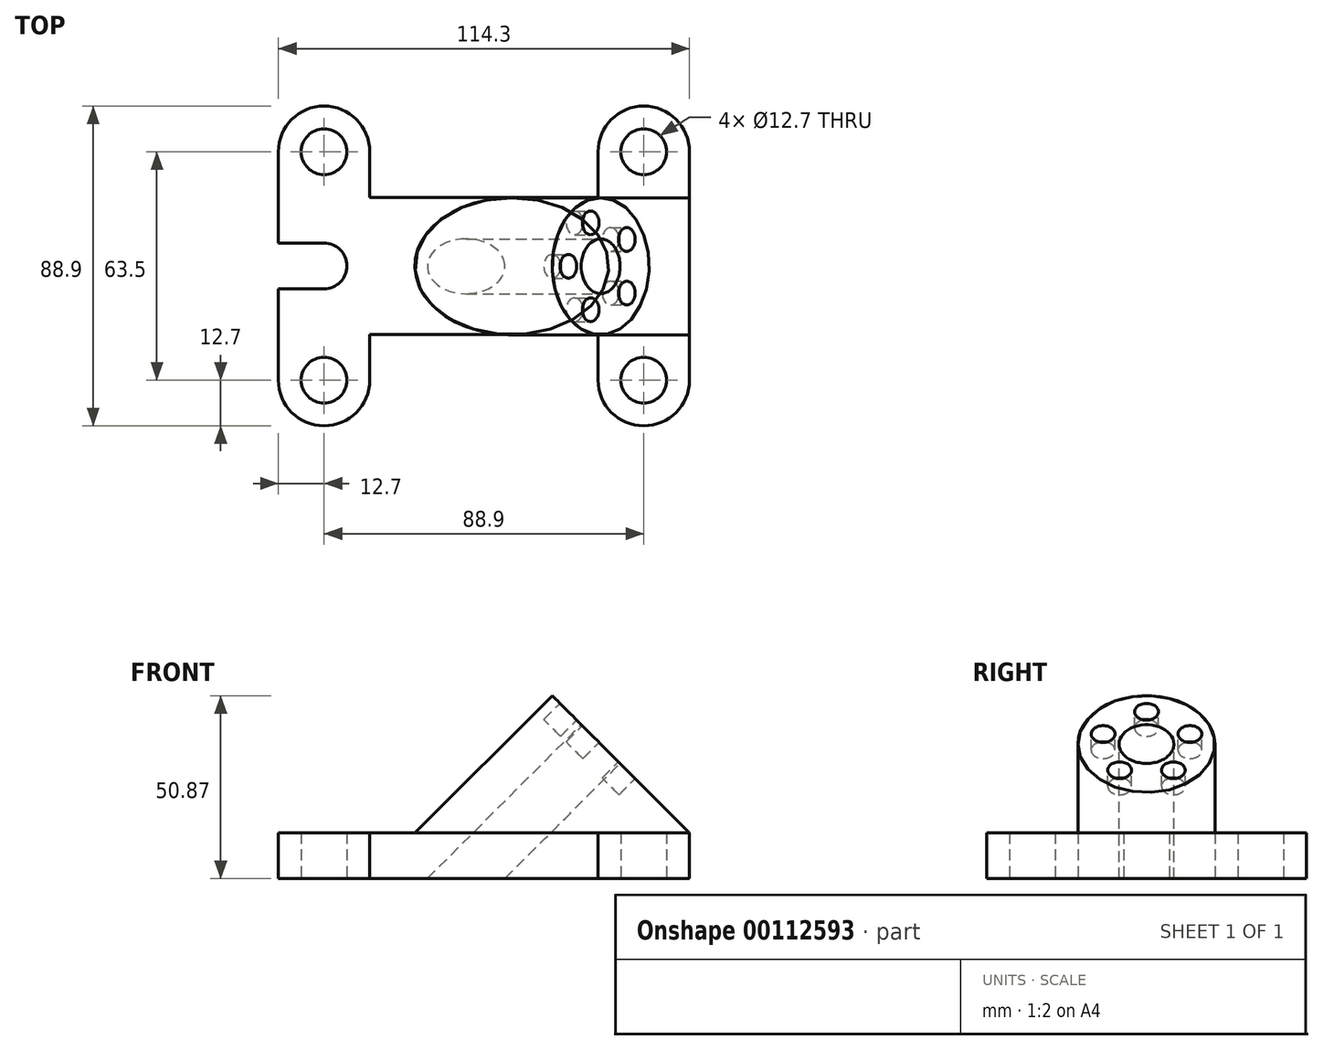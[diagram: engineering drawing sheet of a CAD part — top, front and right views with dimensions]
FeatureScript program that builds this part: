
annotation { "Feature Type Name" : "Feature", "Feature Type Description" : "" }
export const myFeature = defineFeature(function(context is Context, id is Id, definition is map)
    precondition{}
    {
        {
            var Q0;
            Q0=qCreatedBy(makeId("Top.planeOp"),FACE);
            var sketch = newSketch(context, id + "F0", { "sketchPlane" : qUnion([Q0])});
            skLineSegment(sketch, "E0", {"start": v(114.3, 63.5) * mm, "end": v(114.3, 0) * mm});
            skLineSegment(sketch, "E1", {"start": v(0, 38.1) * mm, "end": v(0, 63.5) * mm});
            skLineSegment(sketch, "E2", {"start": v(0, 38.1) * mm, "end": v(12.7, 38.1) * mm});
            skLineSegment(sketch, "E3", {"start": v(0, 0) * mm, "end": v(0, 25.4) * mm});
            skLineSegment(sketch, "E4", {"start": v(0, 25.4) * mm, "end": v(12.7, 25.4) * mm});
            skLineSegment(sketch, "E5", {"start": v(25.4, 63.5) * mm, "end": v(25.4, 50.8) * mm});
            skLineSegment(sketch, "E6", {"start": v(25.4, 50.8) * mm, "end": v(88.9, 50.8) * mm});
            skLineSegment(sketch, "E7", {"start": v(88.9, 50.8) * mm, "end": v(88.9, 63.5) * mm});
            skLineSegment(sketch, "E8", {"start": v(25.4, 0) * mm, "end": v(25.4, 12.7) * mm});
            skLineSegment(sketch, "E9", {"start": v(25.4, 12.7) * mm, "end": v(88.9, 12.7) * mm});
            skLineSegment(sketch, "E10", {"start": v(88.9, 12.7) * mm, "end": v(88.9, 0) * mm});
            skArc(sketch, "E11", {"start": v(25.4, 63.5) * mm, "mid": v(12.7, 76.2) * mm, "end": v(0, 63.5) * mm});
            skArc(sketch, "E12", {"start": v(114.3, 63.5) * mm, "mid": v(101.6, 76.2) * mm, "end": v(88.9, 63.5) * mm});
            skArc(sketch, "E13", {"start": v(88.9, 0) * mm, "mid": v(101.6, -12.7) * mm, "end": v(114.3, 0) * mm});
            skArc(sketch, "E14", {"start": v(0, 0) * mm, "mid": v(12.7, -12.7) * mm, "end": v(25.4, 0) * mm});
            skArc(sketch, "E15", {"start": v(12.7, 25.4) * mm, "mid": v(19.05, 31.75) * mm, "end": v(12.7, 38.1) * mm});
            skCircle(sketch, "E16", {"center": v(12.7, 63.5) * mm, "radius": 6.35 * mm});
            skCircle(sketch, "E17", {"center": v(101.6, 63.5) * mm, "radius": 6.35 * mm});
            skCircle(sketch, "E18", {"center": v(101.6, 0) * mm, "radius": 6.35 * mm});
            skCircle(sketch, "E19", {"center": v(12.7, 0) * mm, "radius": 6.35 * mm});
            skPoint(sketch, "E20", {"position": v(114.3, 31.75) * mm});
            skLineSegment(sketch, "E21", {"start": v(0, 38.1) * mm, "end": v(0, 25.4) * mm, "construction": true});
            skSolve(sketch);
        }
        {
            var Q0;
            Q0=makeQuery(id+"F0.imprint","IMPRINT",FACE,{"disambiguationData":[TD([[makeQuery(id+"F0.imprint","IMPRINT",EDGE,{"derivedFrom":sQuery(id+"F0.wireOp",EDGE,"E0")}),-1.0]])]});
            extrude(context, id + "F1", {"entities" : qUnion([Q0]), "depth" : 12.7 * mm});
        }
        {
            var Q0;
            Q0=makeQuery(id+"F1.opExtrude","CAP_EDGE",EDGE,{"disambiguationData":[OSD([sQuery(id+"F0.wireOp",EDGE,"E0")])],"isStart":false});
            cPlane(context, id + "F2", {"entities" : qUnion([Q0]), "cplaneType" : CPlaneType.LINE_ANGLE, "offset" : 25.4 * mm, "angle" : 135 * degree, "width" : 152.4 * mm, "height" : 152.4 * mm});
        }
        {
            var Q0;
            Q0=qCreatedBy(id+"F2.planeOp",FACE);
            var sketch = newSketch(context, id + "F3", { "sketchPlane" : qUnion([Q0])});
            skLineSegment(sketch, "E22.bottom", {"start": v(12.62, -71.84) * mm, "end": v(50.72, -71.84) * mm});
            skLineSegment(sketch, "E22.top", {"start": v(12.62, -36.92) * mm, "end": v(50.72, -36.92) * mm});
            skLineSegment(sketch, "E22.left", {"start": v(12.62, -71.84) * mm, "end": v(12.62, -36.92) * mm});
            skLineSegment(sketch, "E22.right", {"start": v(50.72, -71.84) * mm, "end": v(50.72, -36.92) * mm});
            skArc(sketch, "E23", {"start": v(50.72, -36.92) * mm, "mid": v(31.67, -17.87) * mm, "end": v(12.62, -36.92) * mm});
            skLineSegment(sketch, "E24", {"start": v(31.67, -36.92) * mm, "end": v(31.67, -17.87) * mm, "construction": true});
            skCircle(sketch, "E25", {"center": v(31.67, -36.92) * mm, "radius": 12.7 * mm, "construction": true});
            skSolve(sketch);
        }
        {
            var Q0;
            Q0=makeQuery(id+"F3.imprint","IMPRINT",FACE,{"disambiguationData":[TD([[makeQuery(id+"F3.imprint","IMPRINT",EDGE,{"derivedFrom":sQuery(id+"F3.wireOp",EDGE,"E22.bottom")}),1.0]])]});
            var Q1;
            {var subQ0=sQuery(id+"F3.wireOp",EDGE,"E23");Q1=makeQuery(id+"F3.imprint","IMPRINT",FACE,{"disambiguationData":[TD([[makeQuery(id+"F3.imprint","IMPRINT",EDGE,{"derivedFrom":subQ0}),1.0]])]});}
            var Q2;
            Q2=makeQuery(id+"F1.opExtrude","CAP_FACE",FACE,{"disambiguationData":[OSD([sQuery(id+"F0.wireOp",EDGE,"E0"),sQuery(id+"F0.wireOp",EDGE,"E1"),sQuery(id+"F0.wireOp",EDGE,"E2"),sQuery(id+"F0.wireOp",EDGE,"E3"),sQuery(id+"F0.wireOp",EDGE,"E4"),sQuery(id+"F0.wireOp",EDGE,"E5"),sQuery(id+"F0.wireOp",EDGE,"E6"),sQuery(id+"F0.wireOp",EDGE,"E7"),sQuery(id+"F0.wireOp",EDGE,"E8"),sQuery(id+"F0.wireOp",EDGE,"E9"),sQuery(id+"F0.wireOp",EDGE,"E10"),sQuery(id+"F0.wireOp",EDGE,"E11"),sQuery(id+"F0.wireOp",EDGE,"E12"),sQuery(id+"F0.wireOp",EDGE,"E13"),sQuery(id+"F0.wireOp",EDGE,"E14"),sQuery(id+"F0.wireOp",EDGE,"E15"),sQuery(id+"F0.wireOp",EDGE,"E16"),sQuery(id+"F0.wireOp",EDGE,"E17"),sQuery(id+"F0.wireOp",EDGE,"E18"),sQuery(id+"F0.wireOp",EDGE,"E19")])],"isStart":false});
            extrude(context, id + "F4", {"entities" : qUnion([Q0, Q1]), "operationType" : NewBodyOperationType.ADD, "endBound" : BoundingType.UP_TO_SURFACE, "oppositeDirection" : true, "endBoundEntityFace" : qUnion([Q2]), "depth" : 25.4 * mm});
        }
        {
            var Q0;
            Q0=makeQuery(id+"F4.opExtrude","CAP_FACE",FACE,{"disambiguationData":[OSD([sQuery(id+"F3.wireOp",EDGE,"E22.bottom"),sQuery(id+"F3.wireOp",EDGE,"E22.left"),sQuery(id+"F3.wireOp",EDGE,"E22.right"),sQuery(id+"F3.wireOp",EDGE,"E23")])],"isStart":true});
            var sketch = newSketch(context, id + "F5", { "sketchPlane" : qUnion([Q0])});
            skLineSegment(sketch, "E26", {"start": v(12.62, -36.92) * mm, "end": v(50.72, -36.92) * mm, "construction": true});
            skLineSegment(sketch, "E27", {"start": v(50.72, -36.92) * mm, "end": v(31.67, -36.92) * mm, "construction": true});
            skLineSegment(sketch, "E28", {"start": v(31.67, -36.92) * mm, "end": v(31.67, -17.87) * mm, "construction": true});
            skCircle(sketch, "E29", {"center": v(31.67, -36.92) * mm, "radius": 7.62 * mm});
            skSolve(sketch);
        }
        {
            var Q0;
            Q0=makeQuery(id+"F5.imprint","IMPRINT",FACE,{"disambiguationData":[TD([[makeQuery(id+"F5.imprint","IMPRINT",EDGE,{"derivedFrom":sQuery(id+"F5.wireOp",EDGE,"E29")}),1.0]])]});
            extrude(context, id + "F6", {"entities" : qUnion([Q0]), "operationType" : NewBodyOperationType.REMOVE, "endBound" : BoundingType.THROUGH_ALL, "oppositeDirection" : true, "depth" : 25.4 * mm});
        }
        {
            var Q0;
            Q0=makeQuery(id+"F4.opExtrude","CAP_FACE",FACE,{"disambiguationData":[OSD([sQuery(id+"F3.wireOp",EDGE,"E22.bottom"),sQuery(id+"F3.wireOp",EDGE,"E22.left"),sQuery(id+"F3.wireOp",EDGE,"E22.right"),sQuery(id+"F3.wireOp",EDGE,"E23")])],"isStart":true});
            var sketch = newSketch(context, id + "F7", { "sketchPlane" : qUnion([Q0])});
            skLineSegment(sketch, "E30", {"start": v(12.62, -36.92) * mm, "end": v(50.72, -36.92) * mm, "construction": true});
            skLineSegment(sketch, "E31", {"start": v(50.72, -36.92) * mm, "end": v(31.67, -36.92) * mm, "construction": true});
            skCircle(sketch, "E32", {"center": v(31.67, -24.22) * mm, "radius": 3.3 * mm});
            skCircle(sketch, "E33", {"center": v(31.67, -36.92) * mm, "radius": 12.7 * mm, "construction": true});
            skCircle(sketch, "E34.1.0", {"center": v(19.6, -33) * mm, "radius": 3.3 * mm});
            skCircle(sketch, "E34.2.0", {"center": v(24.2, -47.2) * mm, "radius": 3.3 * mm});
            skCircle(sketch, "E34.3.0", {"center": v(39.13, -47.2) * mm, "radius": 3.3 * mm});
            skCircle(sketch, "E34.4.0", {"center": v(43.75, -33) * mm, "radius": 3.3 * mm});
            skSolve(sketch);
        }
        {
            var Q0;
            Q0=makeQuery(id+"F7.imprint","IMPRINT",FACE,{"disambiguationData":[TD([[makeQuery(id+"F7.imprint","IMPRINT",EDGE,{"derivedFrom":sQuery(id+"F7.wireOp",EDGE,"E34.4.0")}),1.0]])]});
            var Q1;
            Q1=makeQuery(id+"F7.imprint","IMPRINT",FACE,{"disambiguationData":[TD([[makeQuery(id+"F7.imprint","IMPRINT",EDGE,{"derivedFrom":sQuery(id+"F7.wireOp",EDGE,"E34.2.0")}),1.0]])]});
            var Q2;
            Q2=makeQuery(id+"F7.imprint","IMPRINT",FACE,{"disambiguationData":[TD([[makeQuery(id+"F7.imprint","IMPRINT",EDGE,{"derivedFrom":sQuery(id+"F7.wireOp",EDGE,"E32")}),1.0]])]});
            var Q3;
            Q3=makeQuery(id+"F7.imprint","IMPRINT",FACE,{"disambiguationData":[TD([[makeQuery(id+"F7.imprint","IMPRINT",EDGE,{"derivedFrom":sQuery(id+"F7.wireOp",EDGE,"E34.1.0")}),1.0]])]});
            var Q4;
            Q4=makeQuery(id+"F7.imprint","IMPRINT",FACE,{"disambiguationData":[TD([[makeQuery(id+"F7.imprint","IMPRINT",EDGE,{"derivedFrom":sQuery(id+"F7.wireOp",EDGE,"E34.3.0")}),1.0]])]});
            extrude(context, id + "F8", {"entities" : qUnion([Q0, Q1, Q2, Q3, Q4]), "operationType" : NewBodyOperationType.REMOVE, "oppositeDirection" : true, "depth" : 6.35 * mm});
        }
    });
